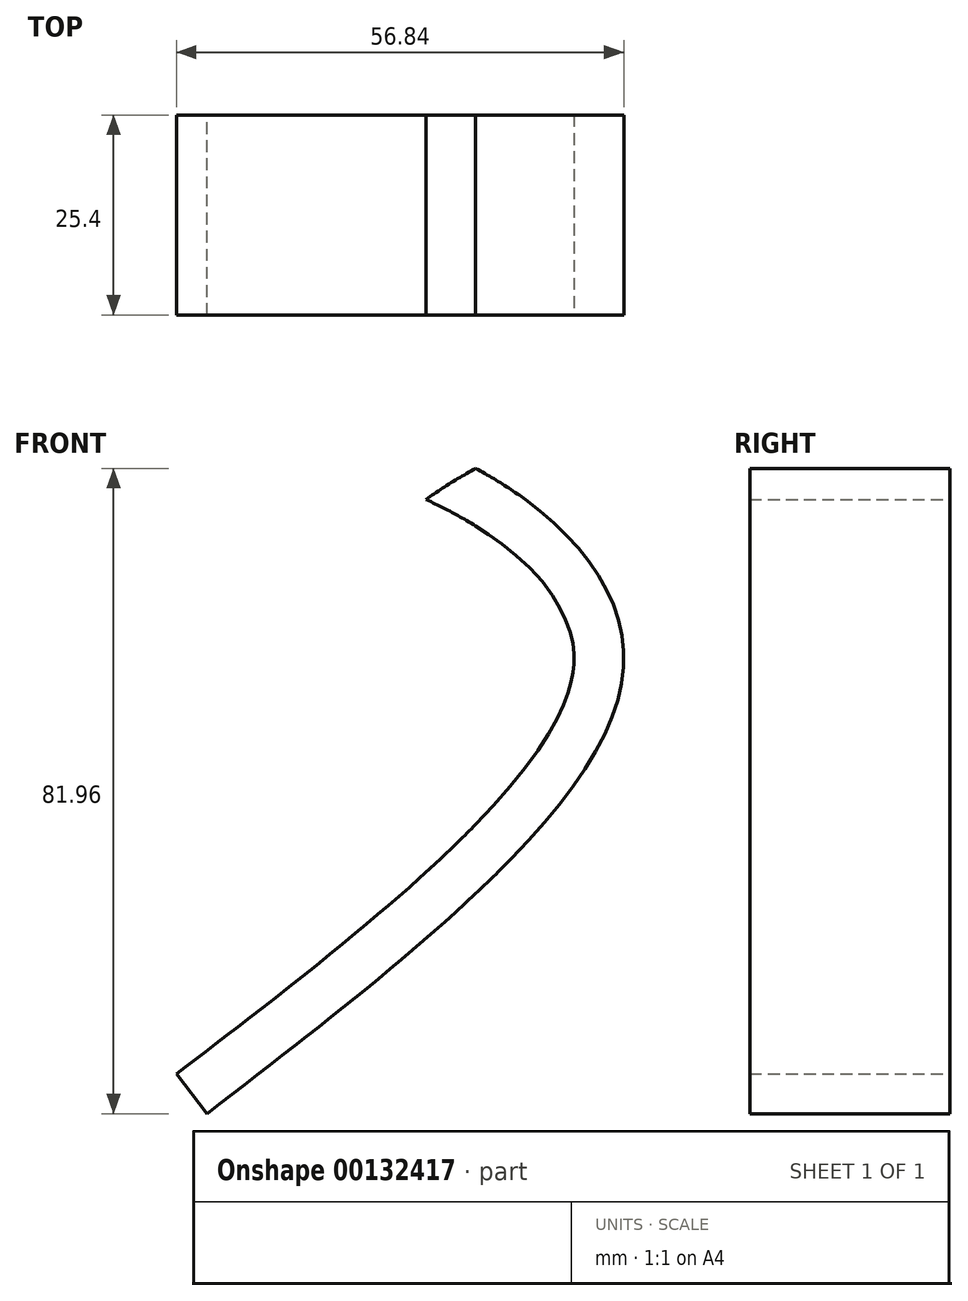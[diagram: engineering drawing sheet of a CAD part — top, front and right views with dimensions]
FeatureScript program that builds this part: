
annotation { "Feature Type Name" : "Feature", "Feature Type Description" : "" }
export const myFeature = defineFeature(function(context is Context, id is Id, definition is map)
    precondition{}
    {
        {
            var Q0;
            Q0=qCreatedBy(makeId("Front.planeOp"),FACE);
            var sketch = newSketch(context, id + "F0", { "sketchPlane" : qUnion([Q0])});
            skFitSpline(sketch, "E0", {"points": [v(34.15, -55.88) * mm, v(-18.72, 0) * mm, v(0, 26.08) * mm, v(23.86, 39.92) * mm, v(11.97, 56.24) * mm, v(0, 61.56) * mm], "startDerivative": vector(-242.83, 186.9) * mm, "endDerivative": vector(-84.78, 24.16) * mm});
            skFitSpline(sketch, "E1.MirrorCS", {"points": [v(-34.15, -55.88) * mm, v(18.72, 0) * mm, v(0, 26.08) * mm, v(-23.86, 39.92) * mm, v(-11.97, 56.24) * mm, v(0, 61.56) * mm], "startDerivative": vector(242.83, 186.9) * mm, "endDerivative": vector(84.78, 24.16) * mm});
            skFitSpline(sketch, "E2.0", {"points": [v(38.02, -50.85) * mm, v(32.96, -46.96) * mm, v(25.41, -41.14) * mm, v(15.98, -33.53) * mm, v(9.36, -27.92) * mm, v(3.36, -22.44) * mm, v(-1.88, -17.14) * mm, v(-6.22, -12.07) * mm, v(-8.95, -8.13) * mm, v(-10.55, -5.22) * mm, v(-11.45, -3.18) * mm, v(-11.96, -1.61) * mm, v(-12.24, -0.45) * mm, v(-12.38, 0.38) * mm, v(-12.45, 1.17) * mm, v(-12.49, 2.22) * mm, v(-12.4, 3.5) * mm, v(-12.07, 5.03) * mm, v(-11.54, 6.6) * mm, v(-10.79, 8.19) * mm, v(-9.48, 10.33) * mm, v(-7.3, 13.02) * mm, v(-4.45, 15.6) * mm, v(-1.85, 17.54) * mm, v(0.24, 18.92) * mm, v(2.08, 20) * mm, v(3.6, 20.8) * mm, v(5.17, 21.6) * mm, v(7.2, 22.54) * mm, v(10.56, 24) * mm, v(13.97, 25.38) * mm, v(17.3, 26.8) * mm, v(19.73, 27.9) * mm, v(22.06, 29.12) * mm, v(24.3, 30.5) * mm, v(26.1, 31.93) * mm, v(27.44, 33.33) * mm, v(28.38, 34.55) * mm, v(29.2, 35.95) * mm, v(29.73, 37.26) * mm, v(30.04, 38.4) * mm, v(30.26, 39.55) * mm, v(30.35, 40.96) * mm, v(30.23, 42.55) * mm, v(29.84, 44.54) * mm, v(29.03, 46.77) * mm, v(27.74, 49.17) * mm, v(26.23, 51.4) * mm, v(24.55, 53.47) * mm, v(22.13, 56.09) * mm, v(18.88, 59.05) * mm, v(14.93, 62) * mm, v(11.2, 64.22) * mm, v(7.7, 65.79) * mm, v(4.5, 66.88) * mm, v(2.62, 67.42) * mm, v(1.74, 67.67) * mm]});
            skLineSegment(sketch, "E3", {"start": v(38.02, -50.85) * mm, "end": v(34.15, -55.88) * mm});
            skFitSpline(sketch, "E4.0", {"points": [v(-38.02, -50.85) * mm, v(-32.96, -46.96) * mm, v(-25.41, -41.14) * mm, v(-15.98, -33.53) * mm, v(-9.36, -27.92) * mm, v(-3.36, -22.44) * mm, v(1.88, -17.14) * mm, v(6.22, -12.07) * mm, v(8.95, -8.13) * mm, v(10.55, -5.22) * mm, v(11.45, -3.18) * mm, v(11.96, -1.61) * mm, v(12.24, -0.45) * mm, v(12.38, 0.38) * mm, v(12.45, 1.17) * mm, v(12.49, 2.22) * mm, v(12.4, 3.5) * mm, v(12.07, 5.03) * mm, v(11.54, 6.6) * mm, v(10.79, 8.19) * mm, v(9.48, 10.33) * mm, v(7.3, 13.02) * mm, v(4.45, 15.6) * mm, v(1.85, 17.54) * mm, v(-0.24, 18.92) * mm, v(-2.08, 20) * mm, v(-3.6, 20.8) * mm, v(-5.17, 21.6) * mm, v(-7.2, 22.54) * mm, v(-10.56, 24) * mm, v(-13.97, 25.38) * mm, v(-17.3, 26.8) * mm, v(-19.73, 27.9) * mm, v(-22.06, 29.12) * mm, v(-24.3, 30.5) * mm, v(-26.1, 31.93) * mm, v(-27.44, 33.33) * mm, v(-28.38, 34.55) * mm, v(-29.2, 35.95) * mm, v(-29.73, 37.26) * mm, v(-30.04, 38.4) * mm, v(-30.26, 39.55) * mm, v(-30.35, 40.96) * mm, v(-30.23, 42.55) * mm, v(-29.84, 44.54) * mm, v(-29.03, 46.77) * mm, v(-27.74, 49.17) * mm, v(-26.23, 51.4) * mm, v(-24.55, 53.47) * mm, v(-22.13, 56.09) * mm, v(-18.88, 59.05) * mm, v(-14.93, 62) * mm, v(-11.2, 64.22) * mm, v(-7.7, 65.79) * mm, v(-4.5, 66.88) * mm, v(-2.62, 67.42) * mm, v(-1.74, 67.67) * mm]});
            skLineSegment(sketch, "E5", {"start": v(-34.15, -55.88) * mm, "end": v(-38.02, -50.85) * mm});
            skArc(sketch, "E6.filletArc", {"start": v(1.74, 67.67) * mm, "mid": v(0, 67.9) * mm, "end": v(-1.74, 67.67) * mm});
            skLineSegment(sketch, "E7", {"start": v(0, 61.56) * mm, "end": v(0, 67.67) * mm});
            skSolve(sketch);
        }
        {
            var Q0;
            {var subQ5=sQuery(id+"F0.wireOp",EDGE,"E5");Q0=makeQuery(id+"F0.imprint","IMPRINT",FACE,{"disambiguationData":[TD([[makeQuery(id+"F0.imprint","IMPRINT",EDGE,{"derivedFrom":subQ5}),-1.0]])]});}
            var Q1;
            {var subQ0=sQuery(id+"F0.wireOp",EDGE,"E1.MirrorCS");var subQ1=sQuery(id+"F0.wireOp",EDGE,"E0");var subQ2=makeQuery(id+"F0.imprint","INTERSECT",VERTEX,{"disambiguationData":[OD(1.0)],"derivedFrom":[subQ1,subQ0]});Q1=makeQuery(id+"F0.imprint","IMPRINT",FACE,{"disambiguationData":[TD([[makeQuery(id+"F0.imprint","IMPRINT",EDGE,{"disambiguationData":[TD([[subQ2,-1.0]])],"derivedFrom":subQ1}),-1.0]])]});}
            var Q2;
            {var subQ0=sQuery(id+"F0.wireOp",EDGE,"E2.0");var subQ1=sQuery(id+"F0.wireOp",EDGE,"E1.MirrorCS");var subQ2=makeQuery(id+"F0.imprint","INTERSECT",VERTEX,{"disambiguationData":[OD(0.0)],"derivedFrom":[subQ1,subQ0]});Q2=makeQuery(id+"F0.imprint","IMPRINT",FACE,{"disambiguationData":[TD([[makeQuery(id+"F0.imprint","IMPRINT",EDGE,{"disambiguationData":[TD([[subQ2,-1.0]])],"derivedFrom":subQ1}),1.0]])]});}
            var Q3;
            {var subQ0=sQuery(id+"F0.wireOp",EDGE,"E4.0");var subQ1=sQuery(id+"F0.wireOp",EDGE,"E0");var subQ2=makeQuery(id+"F0.imprint","INTERSECT",VERTEX,{"disambiguationData":[OD(1.0)],"derivedFrom":[subQ1,subQ0]});Q3=makeQuery(id+"F0.imprint","IMPRINT",FACE,{"disambiguationData":[TD([[makeQuery(id+"F0.imprint","IMPRINT",EDGE,{"disambiguationData":[TD([[subQ2,-1.0]])],"derivedFrom":subQ1}),-1.0]])]});}
            extrude(context, id + "F1", {"entities" : qUnion([Q0, Q1, Q2, Q3]), "depth" : 25.4 * mm});
        }
    });
